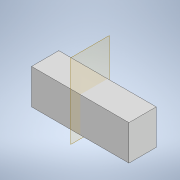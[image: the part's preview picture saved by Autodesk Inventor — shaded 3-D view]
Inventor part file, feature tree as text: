
AUTODESK INVENTOR PART (.ipt)
format: ipt  version: 2022 (Build 260153070, 153G)  size: 94,208 bytes
history: native  units: mm
features: extrude x1, plane x1, sketch x1
ambient origin geometry x8: Origin, YZ Plane, XZ Plane, XY Plane, X Axis, Y Axis, Z Axis, Center Point
bodies: Solid1 (feature_tree)
feature tree (3):
  extrude  "Extrusion1"  Depth=18.0mm
  plane  "Work Plane1"
  sketch  "Sketch1"  dims[d0=50.0mm d1=18.0mm d2=14.0mm d3=0.0mm]
